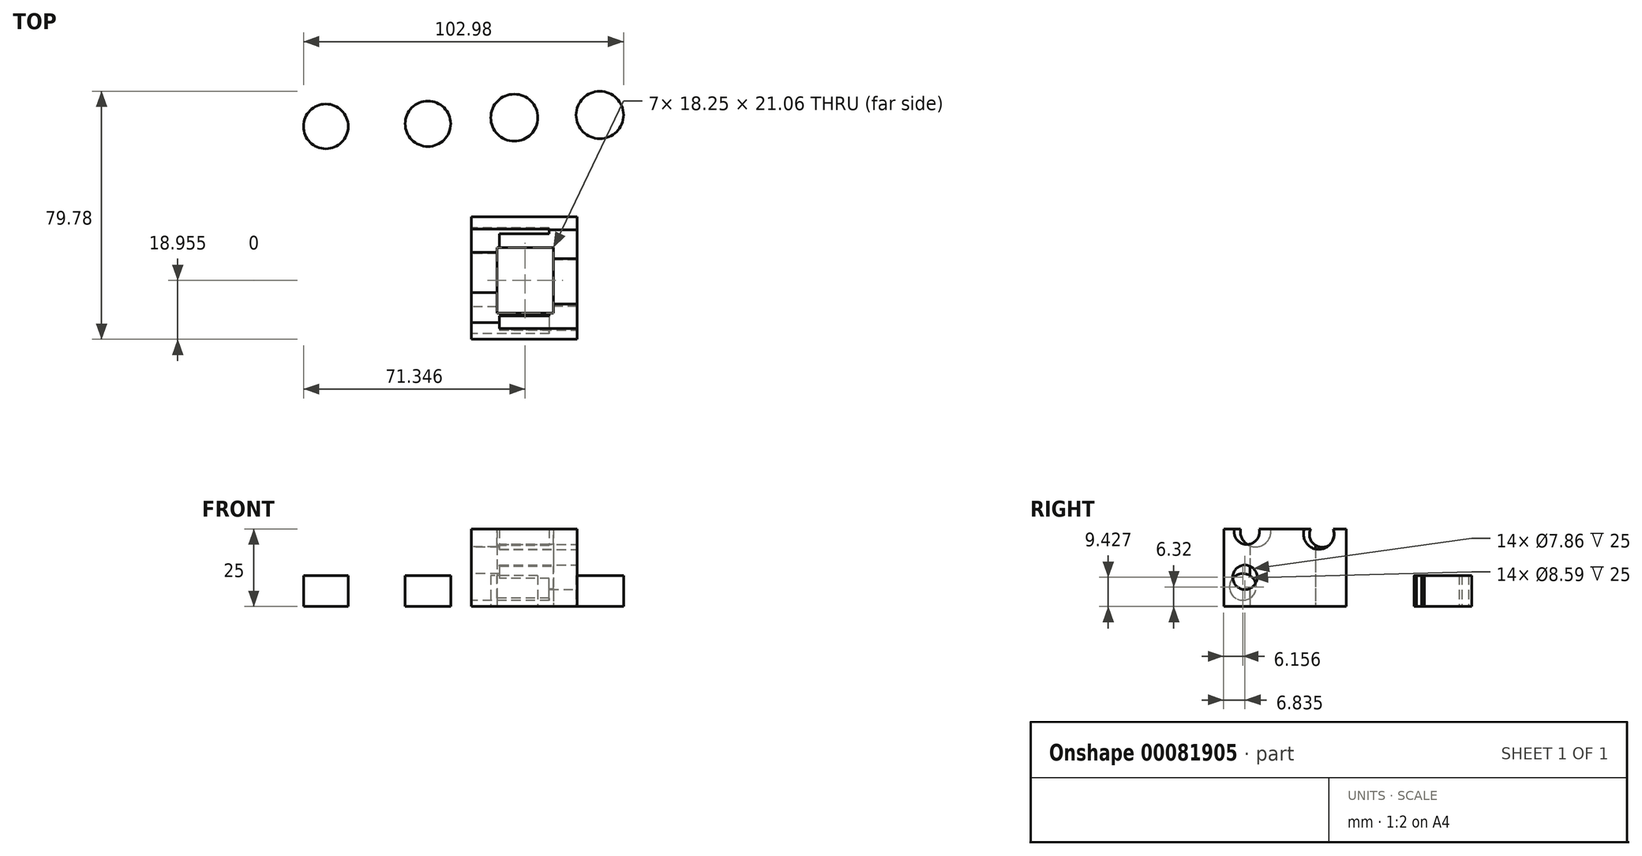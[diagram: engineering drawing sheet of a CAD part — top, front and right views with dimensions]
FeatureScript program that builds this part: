
annotation { "Feature Type Name" : "Feature", "Feature Type Description" : "" }
export const myFeature = defineFeature(function(context is Context, id is Id, definition is map)
    precondition{}
    {
        {
            var Q0;
            Q0=qCreatedBy(makeId("Top.planeOp"),FACE);
            var sketch = newSketch(context, id + "F0", { "sketchPlane" : qUnion([Q0])});
            skLineSegment(sketch, "E0.bottom", {"start": v(0, 0) * mm, "end": v(33.97, 0) * mm});
            skLineSegment(sketch, "E0.top", {"start": v(0, -39.45) * mm, "end": v(33.97, -39.45) * mm});
            skLineSegment(sketch, "E0.left", {"start": v(0, 0) * mm, "end": v(0, -39.45) * mm});
            skLineSegment(sketch, "E0.right", {"start": v(33.97, 0) * mm, "end": v(33.97, -39.45) * mm});
            skLineSegment(sketch, "E1.bottom", {"start": v(8.14, -9.97) * mm, "end": v(26.4, -9.97) * mm});
            skLineSegment(sketch, "E1.top", {"start": v(8.14, -31.02) * mm, "end": v(26.4, -31.02) * mm});
            skLineSegment(sketch, "E1.left", {"start": v(8.14, -9.97) * mm, "end": v(8.14, -31.02) * mm});
            skLineSegment(sketch, "E1.right", {"start": v(26.4, -9.97) * mm, "end": v(26.4, -31.02) * mm});
            skSolve(sketch);
        }
        {
            var Q0;
            Q0=qCreatedBy(makeId("Top.planeOp"),FACE);
            var sketch = newSketch(context, id + "F1", { "sketchPlane" : qUnion([Q0])});
            skCircle(sketch, "E2", {"center": v(-46.89, 29.06) * mm, "radius": 7.2 * mm});
            skCircle(sketch, "E3", {"center": v(-14.04, 29.9) * mm, "radius": 7.32 * mm});
            skCircle(sketch, "E4", {"center": v(13.76, 31.86) * mm, "radius": 7.56 * mm});
            skCircle(sketch, "E5", {"center": v(41.27, 32.7) * mm, "radius": 7.63 * mm});
            skSolve(sketch);
        }
        {
            var Q0;
            Q0 = qSketchRegion(id + "F1", true);
            extrude(context, id + "F2", {"entities" : qUnion([Q0]), "depth" : 10 * mm});
        }
        {
            var Q0;
            Q0=makeQuery(id+"F0.imprint","IMPRINT",FACE,{"disambiguationData":[TD([[makeQuery(id+"F0.imprint","IMPRINT",EDGE,{"derivedFrom":sQuery(id+"F0.wireOp",EDGE,"E0.bottom")}),-1.0]])]});
            extrude(context, id + "F3", {"entities" : qUnion([Q0]), "depth" : 25 * mm});
        }
        {
            var Q0;
            Q0=makeQuery(id+"F3.opExtrude","SWEPT_FACE",FACE,{"disambiguationData":[OSD([sQuery(id+"F0.wireOp",EDGE,"E0.right")])]});
            var sketch = newSketch(context, id + "F4", { "sketchPlane" : qUnion([Q0])});
            skArc(sketch, "E6", {"start": v(-13.46, 25) * mm, "mid": v(-8.85, 18.35) * mm, "end": v(-4.24, 25) * mm});
            skArc(sketch, "E7", {"start": v(-35.95, 25) * mm, "mid": v(-32.01, 19.96) * mm, "end": v(-28.07, 25) * mm});
            skArc(sketch, "E8", {"start": v(-35.95, 25) * mm, "mid": v(-32.01, 19.99) * mm, "end": v(-28.07, 25) * mm});
            skArc(sketch, "E9", {"start": v(-13.46, 25) * mm, "mid": v(-8.85, 18.41) * mm, "end": v(-4.24, 25) * mm});
            skSolve(sketch);
        }
        {
            var Q0;
            {var subQ0=sQuery(id+"F4.wireOp",EDGE,"E9");Q0=makeQuery(id+"F4.imprint","IMPRINT",FACE,{"disambiguationData":[TD([[makeQuery(id+"F4.imprint","IMPRINT",EDGE,{"derivedFrom":subQ0}),1.0]])]});}
            var Q1;
            {var subQ0=sQuery(id+"F4.wireOp",EDGE,"E8");Q1=makeQuery(id+"F4.imprint","IMPRINT",FACE,{"disambiguationData":[TD([[makeQuery(id+"F4.imprint","IMPRINT",EDGE,{"derivedFrom":subQ0}),1.0]])]});}
            extrude(context, id + "F5", {"entities" : qUnion([Q0, Q1]), "operationType" : NewBodyOperationType.REMOVE, "oppositeDirection" : true, "depth" : 25 * mm});
        }
        {
            var Q0;
            Q0=makeQuery(id+"F3.opExtrude","SWEPT_FACE",FACE,{"disambiguationData":[OSD([sQuery(id+"F0.wireOp",EDGE,"E0.left")])]});
            var sketch = newSketch(context, id + "F6", { "sketchPlane" : qUnion([Q0])});
            skArc(sketch, "E10", {"start": v(24.37, 25) * mm, "mid": v(29.2, 19.2) * mm, "end": v(34.02, 25) * mm});
            skArc(sketch, "E11", {"start": v(4, 25) * mm, "mid": v(7.74, 19.08) * mm, "end": v(11.47, 25) * mm});
            skSolve(sketch);
        }
        {
            var Q0;
            {var subQ0=sQuery(id+"F6.wireOp",EDGE,"E10");Q0=makeQuery(id+"F6.imprint","IMPRINT",FACE,{"disambiguationData":[TD([[makeQuery(id+"F6.imprint","IMPRINT",EDGE,{"derivedFrom":subQ0}),1.0]])]});}
            var Q1;
            {var subQ0=sQuery(id+"F6.wireOp",EDGE,"E11");Q1=makeQuery(id+"F6.imprint","IMPRINT",FACE,{"disambiguationData":[TD([[makeQuery(id+"F6.imprint","IMPRINT",EDGE,{"derivedFrom":subQ0}),1.0]])]});}
            extrude(context, id + "F7", {"entities" : qUnion([Q0, Q1]), "operationType" : NewBodyOperationType.REMOVE, "oppositeDirection" : true, "depth" : 25 * mm});
        }
        {
            var Q0;
            Q0=makeQuery(id+"F3.opExtrude","SWEPT_FACE",FACE,{"disambiguationData":[OSD([sQuery(id+"F0.wireOp",EDGE,"E0.left")])]});
            var sketch = newSketch(context, id + "F8", { "sketchPlane" : qUnion([Q0])});
            skCircle(sketch, "E12", {"center": v(33.97, 8.56) * mm, "radius": 4.21 * mm});
            skSolve(sketch);
        }
        {
            var Q0;
            Q0=makeQuery(id+"F3.opExtrude","SWEPT_FACE",FACE,{"disambiguationData":[OSD([sQuery(id+"F0.wireOp",EDGE,"E0.right")])]});
            var sketch = newSketch(context, id + "F9", { "sketchPlane" : qUnion([Q0])});
            skCircle(sketch, "E13", {"center": v(-32.62, 9.43) * mm, "radius": 3.93 * mm});
            skSolve(sketch);
        }
        {
            var Q0;
            Q0=makeQuery(id+"F9.imprint","IMPRINT",FACE,{"disambiguationData":[TD([[makeQuery(id+"F9.imprint","IMPRINT",EDGE,{"derivedFrom":sQuery(id+"F9.wireOp",EDGE,"E13")}),1.0]])]});
            var Q1;
            Q1=makeQuery(id+"F8.imprint","IMPRINT",FACE,{"disambiguationData":[TD([[makeQuery(id+"F8.imprint","IMPRINT",EDGE,{"derivedFrom":sQuery(id+"F8.wireOp",EDGE,"E12")}),1.0]])]});
            extrude(context, id + "F10", {"entities" : qUnion([Q0, Q1]), "operationType" : NewBodyOperationType.REMOVE, "oppositeDirection" : true, "depth" : 25 * mm});
        }
        {
            var Q0;
            Q0=makeQuery(id+"F3.opExtrude","SWEPT_FACE",FACE,{"disambiguationData":[OSD([sQuery(id+"F0.wireOp",EDGE,"E0.left")])]});
            var sketch = newSketch(context, id + "F11", { "sketchPlane" : qUnion([Q0])});
            skCircle(sketch, "E14", {"center": v(33.3, 6.32) * mm, "radius": 4.3 * mm});
            skSolve(sketch);
        }
        {
            var Q0;
            Q0=makeQuery(id+"F11.imprint","IMPRINT",FACE,{"disambiguationData":[TD([[makeQuery(id+"F11.imprint","IMPRINT",EDGE,{"derivedFrom":sQuery(id+"F11.wireOp",EDGE,"E14")}),1.0]])]});
            extrude(context, id + "F12", {"entities" : qUnion([Q0]), "operationType" : NewBodyOperationType.REMOVE, "oppositeDirection" : true, "depth" : 25 * mm});
        }
    });
